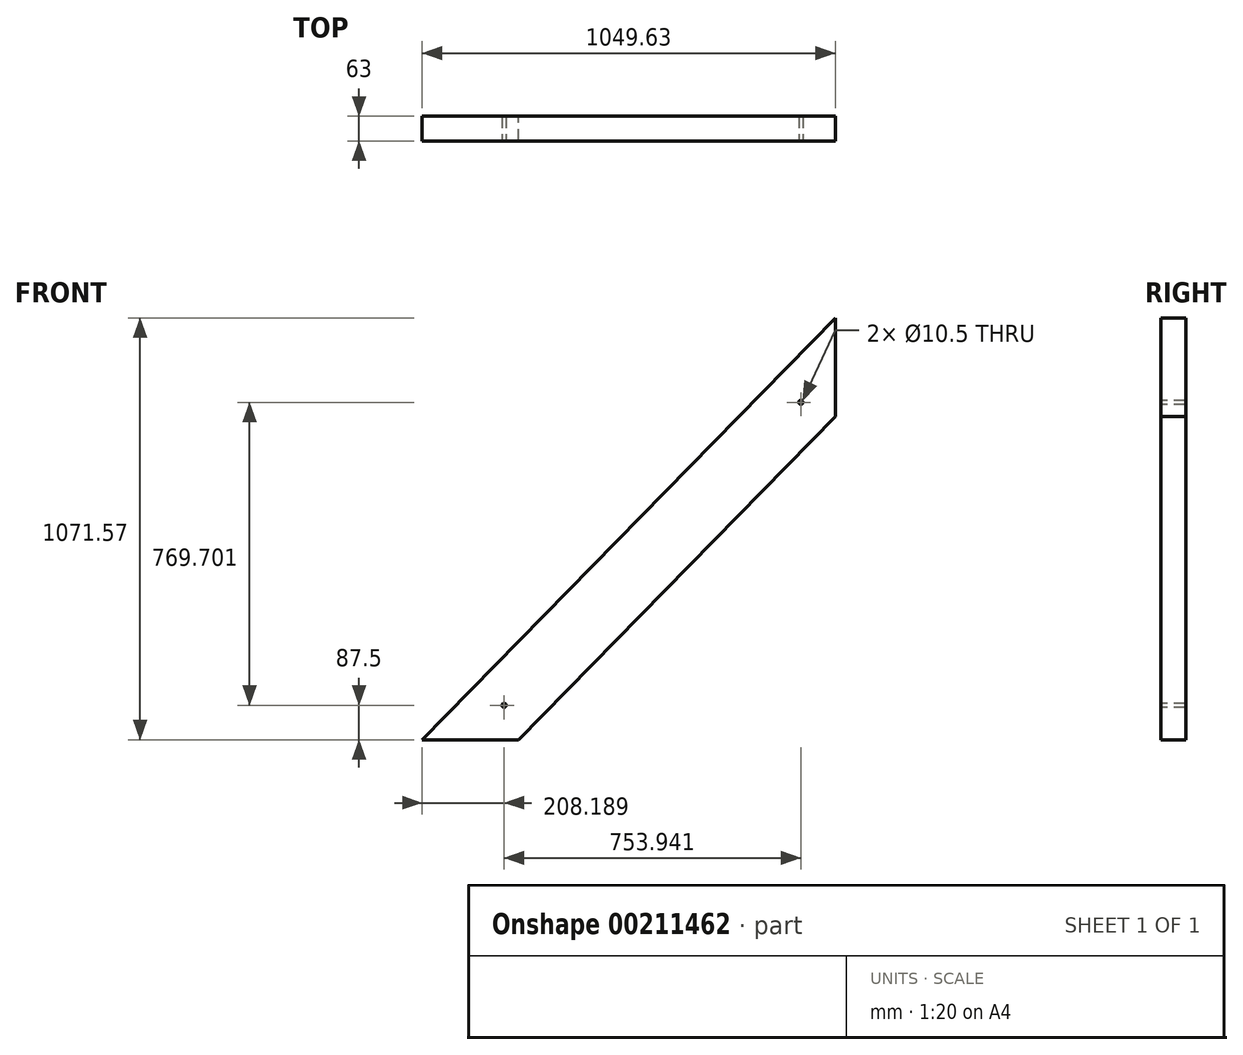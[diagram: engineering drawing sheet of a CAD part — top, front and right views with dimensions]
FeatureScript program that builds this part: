
annotation { "Feature Type Name" : "Feature", "Feature Type Description" : "" }
export const myFeature = defineFeature(function(context is Context, id is Id, definition is map)
    precondition{}
    {
        {
            var Q0;
            Q0=qCreatedBy(makeId("Front.planeOp"),FACE);
            var sketch = newSketch(context, id + "F0", { "sketchPlane" : qUnion([Q0])});
            skLineSegment(sketch, "E0", {"start": v(-1049.63, 0) * mm, "end": v(-804.67, 0) * mm});
            skLineSegment(sketch, "E1", {"start": v(-804.67, 0) * mm, "end": v(0, 821.49) * mm});
            skLineSegment(sketch, "E2", {"start": v(0, 821.49) * mm, "end": v(0, 1071.57) * mm});
            skLineSegment(sketch, "E3", {"start": v(0, 1071.57) * mm, "end": v(-1049.63, 0) * mm});
            skSolve(sketch);
        }
        {
            var Q0;
            Q0=qSketchRegion(id+"F0",true);
            extrude(context, id + "F1", {"entities" : qUnion([Q0]), "depth" : 63 * mm});
        }
        {
            var Q0;
            Q0=makeQuery(id+"F1.opExtrude","CAP_FACE",FACE,{"disambiguationData":[OSD([sQuery(id+"F0.wireOp",EDGE,"E0"),sQuery(id+"F0.wireOp",EDGE,"E1"),sQuery(id+"F0.wireOp",EDGE,"E2"),sQuery(id+"F0.wireOp",EDGE,"E3")])],"isStart":false});
            var sketch = newSketch(context, id + "F2", { "sketchPlane" : qUnion([Q0])});
            skLineSegment(sketch, "E4", {"start": v(0, -12.22) * mm, "end": v(-947.17, 915.56) * mm, "construction": true});
            skLineSegment(sketch, "E5", {"start": v(-927.15, 0) * mm, "end": v(0, 946.53) * mm, "construction": true});
            skCircle(sketch, "E6", {"center": v(-841.44, 87.5) * mm, "radius": 5.25 * mm});
            skCircle(sketch, "E7", {"center": v(-87.5, 857.2) * mm, "radius": 5.25 * mm});
            skSolve(sketch);
        }
        {
            var Q0;
            Q0 = qSketchRegion(id + "F2", true);
            extrude(context, id + "F3", {"entities" : qUnion([Q0]), "operationType" : NewBodyOperationType.REMOVE, "endBound" : BoundingType.THROUGH_ALL, "oppositeDirection" : true, "depth" : 25 * mm});
        }
    });
